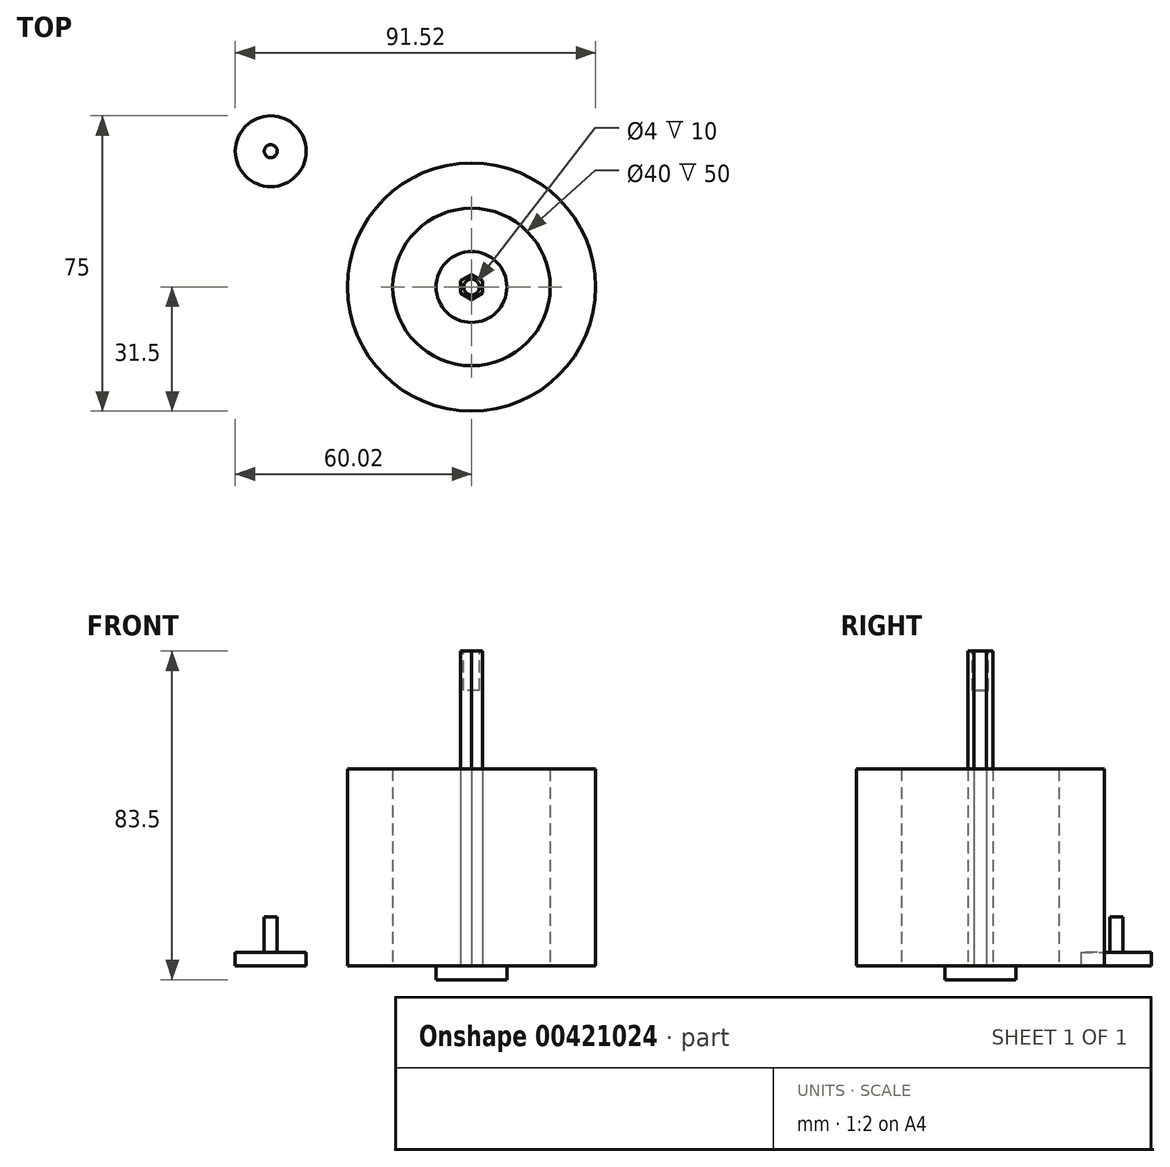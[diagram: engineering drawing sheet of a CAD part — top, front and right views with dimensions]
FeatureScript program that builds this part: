
annotation { "Feature Type Name" : "Feature", "Feature Type Description" : "" }
export const myFeature = defineFeature(function(context is Context, id is Id, definition is map)
    precondition{}
    {
        {
            var Q0;
            Q0=qCreatedBy(makeId("Top.planeOp"),FACE);
            var sketch = newSketch(context, id + "F0", { "sketchPlane" : qUnion([Q0])});
            skCircle(sketch, "E0", {"center": v(0, 0) * mm, "radius": 31.5 * mm});
            skCircle(sketch, "E1", {"center": v(0, 0) * mm, "radius": 20 * mm});
            skSolve(sketch);
        }
        {
            var Q0;
            Q0 = qSketchRegion(id + "F0", true);
            extrude(context, id + "F1", {"entities" : qUnion([Q0]), "depth" : 50 * mm});
        }
        {
            var Q0;
            Q0=qCreatedBy(makeId("Top.planeOp"),FACE);
            var sketch = newSketch(context, id + "F2", { "sketchPlane" : qUnion([Q0])});
            skCircle(sketch, "E2.cCircle", {"center": v(0, 0) * mm, "radius": 2.75 * mm, "construction": true});
            skLineSegment(sketch, "E2.0", {"start": v(2.75, 1.59) * mm, "end": v(2.75, -1.59) * mm});
            skLineSegment(sketch, "E2.1", {"start": v(2.75, -1.59) * mm, "end": v(0, -3.18) * mm});
            skLineSegment(sketch, "E2.2", {"start": v(0, -3.18) * mm, "end": v(-2.75, -1.59) * mm});
            skLineSegment(sketch, "E2.3", {"start": v(-2.75, -1.59) * mm, "end": v(-2.75, 1.59) * mm});
            skLineSegment(sketch, "E2.4", {"start": v(-2.75, 1.59) * mm, "end": v(0, 3.18) * mm});
            skLineSegment(sketch, "E2.5", {"start": v(0, 3.18) * mm, "end": v(2.75, 1.59) * mm});
            skPoint(sketch, "E2.0.midPoint", {"position": v(2.75, 0) * mm});
            skSolve(sketch);
        }
        {
            var Q0;
            Q0 = qSketchRegion(id + "F2", true);
            extrude(context, id + "F3", {"entities" : qUnion([Q0]), "depth" : 80 * mm});
        }
        {
            var Q0;
            Q0=makeQuery(id+"F3.opExtrude","CAP_FACE",FACE,{"disambiguationData":[OSD([sQuery(id+"F2.wireOp",EDGE,"E2.0"),sQuery(id+"F2.wireOp",EDGE,"E2.1"),sQuery(id+"F2.wireOp",EDGE,"E2.2"),sQuery(id+"F2.wireOp",EDGE,"E2.3"),sQuery(id+"F2.wireOp",EDGE,"E2.4"),sQuery(id+"F2.wireOp",EDGE,"E2.5")])],"isStart":true});
            var sketch = newSketch(context, id + "F4", { "sketchPlane" : qUnion([Q0])});
            skCircle(sketch, "E3", {"center": v(0, 0) * mm, "radius": 9 * mm});
            skSolve(sketch);
        }
        {
            var Q0;
            Q0 = qSketchRegion(id + "F4", true);
            extrude(context, id + "F5", {"entities" : qUnion([Q0]), "operationType" : NewBodyOperationType.ADD, "depth" : 3.5 * mm});
        }
        {
            var Q0;
            Q0=makeQuery(id+"F3.opExtrude","CAP_FACE",FACE,{"disambiguationData":[OSD([sQuery(id+"F2.wireOp",EDGE,"E2.0"),sQuery(id+"F2.wireOp",EDGE,"E2.1"),sQuery(id+"F2.wireOp",EDGE,"E2.2"),sQuery(id+"F2.wireOp",EDGE,"E2.3"),sQuery(id+"F2.wireOp",EDGE,"E2.4"),sQuery(id+"F2.wireOp",EDGE,"E2.5")])],"isStart":false});
            var sketch = newSketch(context, id + "F6", { "sketchPlane" : qUnion([Q0])});
            skCircle(sketch, "E4", {"center": v(0, 0) * mm, "radius": 2 * mm});
            skSolve(sketch);
        }
        {
            var Q0;
            Q0 = qSketchRegion(id + "F6", true);
            extrude(context, id + "F7", {"entities" : qUnion([Q0]), "operationType" : NewBodyOperationType.REMOVE, "oppositeDirection" : true, "depth" : 10 * mm});
        }
        {
            var Q0;
            Q0=qCreatedBy(makeId("Top.planeOp"),FACE);
            var sketch = newSketch(context, id + "F8", { "sketchPlane" : qUnion([Q0])});
            skCircle(sketch, "E5", {"center": v(-51.02, 34.5) * mm, "radius": 9 * mm});
            skSolve(sketch);
        }
        {
            var Q0;
            Q0 = qSketchRegion(id + "F8", true);
            extrude(context, id + "F9", {"entities" : qUnion([Q0]), "depth" : 3.5 * mm});
        }
        {
            var Q0;
            Q0=makeQuery(id+"F9.opExtrude","CAP_FACE",FACE,{"disambiguationData":[OSD([sQuery(id+"F8.wireOp",EDGE,"E5")])],"isStart":false});
            var sketch = newSketch(context, id + "F10", { "sketchPlane" : qUnion([Q0])});
            skCircle(sketch, "E6", {"center": v(-51.02, 34.5) * mm, "radius": 1.65 * mm});
            skSolve(sketch);
        }
        {
            var Q0;
            Q0 = qSketchRegion(id + "F10", true);
            extrude(context, id + "F11", {"entities" : qUnion([Q0]), "operationType" : NewBodyOperationType.ADD, "depth" : 9 * mm});
        }
    });
